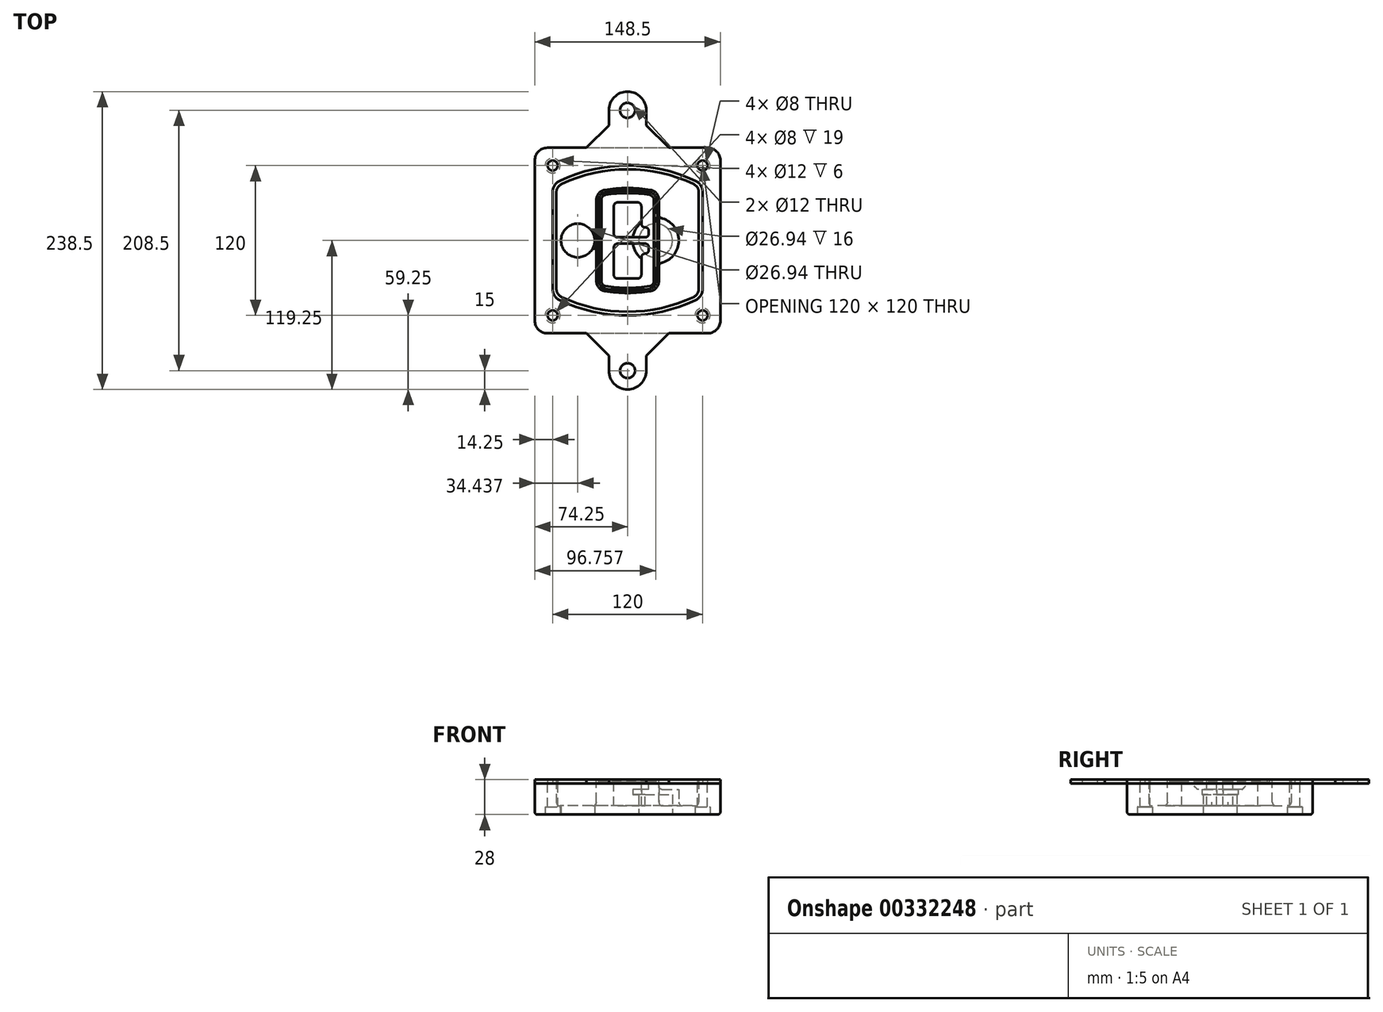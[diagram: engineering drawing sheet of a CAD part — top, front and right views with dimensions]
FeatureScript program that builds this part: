
annotation { "Feature Type Name" : "Feature", "Feature Type Description" : "" }
export const myFeature = defineFeature(function(context is Context, id is Id, definition is map)
    precondition{}
    {
        {
            var Q0;
            Q0=qCreatedBy(makeId("Top.planeOp"),FACE);
            var sketch = newSketch(context, id + "F0", { "sketchPlane" : qUnion([Q0])});
            skPoint(sketch, "E0.rect.middle", {"position": v(0, 0) * mm});
            skLineSegment(sketch, "E1.bottom", {"start": v(-64.25, -74.25) * mm, "end": v(64.25, -74.25) * mm});
            skLineSegment(sketch, "E1.top", {"start": v(-64.25, 74.25) * mm, "end": v(64.25, 74.25) * mm});
            skLineSegment(sketch, "E1.left", {"start": v(-74.25, -64.25) * mm, "end": v(-74.25, 64.25) * mm});
            skLineSegment(sketch, "E1.right", {"start": v(74.25, -64.25) * mm, "end": v(74.25, 64.25) * mm});
            skLineSegment(sketch, "E2", {"start": v(-74.25, 74.25) * mm, "end": v(74.25, -74.25) * mm, "construction": true});
            skLineSegment(sketch, "E3", {"start": v(74.25, 74.25) * mm, "end": v(-74.25, -74.25) * mm, "construction": true});
            skCircle(sketch, "E4", {"center": v(-60, 60) * mm, "radius": 4 * mm});
            skCircle(sketch, "E5", {"center": v(60, 60) * mm, "radius": 4 * mm});
            skCircle(sketch, "E6", {"center": v(60, -60) * mm, "radius": 4 * mm});
            skCircle(sketch, "E7", {"center": v(-60, -60) * mm, "radius": 4 * mm});
            skLineSegment(sketch, "E8", {"start": v(-60, 60) * mm, "end": v(60, 60) * mm, "construction": true});
            skLineSegment(sketch, "E9", {"start": v(60, 60) * mm, "end": v(60, -60) * mm, "construction": true});
            skLineSegment(sketch, "E10", {"start": v(60, -60) * mm, "end": v(-60, -60) * mm, "construction": true});
            skLineSegment(sketch, "E11", {"start": v(-60, -60) * mm, "end": v(-60, 60) * mm, "construction": true});
            skLineSegment(sketch, "E12", {"start": v(-60, 38.83) * mm, "end": v(-60, -38.83) * mm});
            skLineSegment(sketch, "E13", {"start": v(60, 38.83) * mm, "end": v(60, -38.83) * mm});
            skArc(sketch, "E14", {"start": v(54.26, 47.88) * mm, "mid": v(0, 60) * mm, "end": v(-54.26, 47.88) * mm});
            skArc(sketch, "E15", {"start": v(-54.26, -47.88) * mm, "mid": v(0, -60) * mm, "end": v(54.26, -47.88) * mm});
            skLineSegment(sketch, "E16", {"start": v(-60, 0) * mm, "end": v(60, 0) * mm, "construction": true});
            skPoint(sketch, "E17.visualSharp", {"position": v(-60, -45) * mm});
            skArc(sketch, "E17.filletArc", {"start": v(-60, -38.83) * mm, "mid": v(-58.44, -44.2) * mm, "end": v(-54.26, -47.88) * mm});
            skPoint(sketch, "E18.visualSharp", {"position": v(-60, 45) * mm});
            skArc(sketch, "E18.filletArc", {"start": v(-54.26, 47.88) * mm, "mid": v(-58.44, 44.2) * mm, "end": v(-60, 38.83) * mm});
            skPoint(sketch, "E19.visualSharp", {"position": v(60, 45) * mm});
            skArc(sketch, "E19.filletArc", {"start": v(60, 38.83) * mm, "mid": v(58.44, 44.2) * mm, "end": v(54.26, 47.88) * mm});
            skPoint(sketch, "E20.visualSharp", {"position": v(60, -45) * mm});
            skArc(sketch, "E20.filletArc", {"start": v(54.26, -47.88) * mm, "mid": v(58.44, -44.2) * mm, "end": v(60, -38.83) * mm});
            skPoint(sketch, "E21.visualSharp", {"position": v(-74.25, 74.25) * mm});
            skArc(sketch, "E21.filletArc", {"start": v(-64.25, 74.25) * mm, "mid": v(-71.32, 71.32) * mm, "end": v(-74.25, 64.25) * mm});
            skPoint(sketch, "E22.visualSharp", {"position": v(74.25, 74.25) * mm});
            skArc(sketch, "E22.filletArc", {"start": v(74.25, 64.25) * mm, "mid": v(71.32, 71.32) * mm, "end": v(64.25, 74.25) * mm});
            skPoint(sketch, "E23.visualSharp", {"position": v(74.25, -74.25) * mm});
            skArc(sketch, "E23.filletArc", {"start": v(64.25, -74.25) * mm, "mid": v(71.32, -71.32) * mm, "end": v(74.25, -64.25) * mm});
            skPoint(sketch, "E24.visualSharp", {"position": v(-74.25, -74.25) * mm});
            skArc(sketch, "E24.filletArc", {"start": v(-74.25, -64.25) * mm, "mid": v(-71.32, -71.32) * mm, "end": v(-64.25, -74.25) * mm});
            skArc(sketch, "E25.0", {"start": v(57, 38.83) * mm, "mid": v(55.9, 42.58) * mm, "end": v(52.98, 45.17) * mm});
            skLineSegment(sketch, "E25.1", {"start": v(57, 38.83) * mm, "end": v(57, -38.83) * mm});
            skArc(sketch, "E25.2", {"start": v(52.98, -45.17) * mm, "mid": v(55.9, -42.58) * mm, "end": v(57, -38.83) * mm});
            skArc(sketch, "E25.3", {"start": v(-52.98, -45.17) * mm, "mid": v(0, -57) * mm, "end": v(52.98, -45.17) * mm});
            skArc(sketch, "E25.4", {"start": v(-57, -38.83) * mm, "mid": v(-55.9, -42.58) * mm, "end": v(-52.98, -45.17) * mm});
            skArc(sketch, "E25.5", {"start": v(52.98, 45.17) * mm, "mid": v(0, 57) * mm, "end": v(-52.98, 45.17) * mm});
            skLineSegment(sketch, "E25.6", {"start": v(-57, 38.83) * mm, "end": v(-57, -38.83) * mm});
            skArc(sketch, "E25.7", {"start": v(-52.98, 45.17) * mm, "mid": v(-55.9, 42.58) * mm, "end": v(-57, 38.83) * mm});
            skArc(sketch, "E26.0", {"start": v(-55.96, 51.5) * mm, "mid": v(-61.82, 46.33) * mm, "end": v(-64, 38.83) * mm});
            skArc(sketch, "E26.1", {"start": v(55.96, 51.5) * mm, "mid": v(0, 64) * mm, "end": v(-55.96, 51.5) * mm});
            skArc(sketch, "E26.2", {"start": v(64, 38.83) * mm, "mid": v(61.82, 46.33) * mm, "end": v(55.96, 51.5) * mm});
            skLineSegment(sketch, "E26.3", {"start": v(64, 38.83) * mm, "end": v(64, -38.83) * mm});
            skArc(sketch, "E26.4", {"start": v(55.96, -51.5) * mm, "mid": v(61.82, -46.33) * mm, "end": v(64, -38.83) * mm});
            skLineSegment(sketch, "E26.5", {"start": v(-64, 38.83) * mm, "end": v(-64, -38.83) * mm});
            skArc(sketch, "E26.6", {"start": v(-55.96, -51.5) * mm, "mid": v(0, -64) * mm, "end": v(55.96, -51.5) * mm});
            skArc(sketch, "E26.7", {"start": v(-64, -38.83) * mm, "mid": v(-61.82, -46.33) * mm, "end": v(-55.96, -51.5) * mm});
            skSolve(sketch);
        }
        {
            var Q0;
            Q0=makeQuery(id+"F0.imprint","IMPRINT",FACE,{"disambiguationData":[TD([[makeQuery(id+"F0.imprint","IMPRINT",EDGE,{"derivedFrom":sQuery(id+"F0.wireOp",EDGE,"E1.bottom")}),1.0]])]});
            var Q1;
            Q1=makeQuery(id+"F0.imprint","IMPRINT",FACE,{"disambiguationData":[TD([[makeQuery(id+"F0.imprint","IMPRINT",EDGE,{"derivedFrom":sQuery(id+"F0.wireOp",EDGE,"E12")}),1.0]])]});
            var Q2;
            Q2=makeQuery(id+"F0.imprint","IMPRINT",FACE,{"disambiguationData":[TD([[makeQuery(id+"F0.imprint","IMPRINT",EDGE,{"derivedFrom":sQuery(id+"F0.wireOp",EDGE,"E25.0")}),1.0]])]});
            var Q3;
            Q3=makeQuery(id+"F0.imprint","IMPRINT",FACE,{"disambiguationData":[TD([[makeQuery(id+"F0.imprint","IMPRINT",EDGE,{"derivedFrom":sQuery(id+"F0.wireOp",EDGE,"E12")}),-1.0]])]});
            extrude(context, id + "F1", {"entities" : qUnion([Q0, Q1, Q2, Q3]), "oppositeDirection" : true, "depth" : 25 * mm});
        }
        {
            var Q0;
            Q0=makeQuery(id+"F0.imprint","IMPRINT",FACE,{"disambiguationData":[TD([[makeQuery(id+"F0.imprint","IMPRINT",EDGE,{"derivedFrom":sQuery(id+"F0.wireOp",EDGE,"E12")}),1.0]])]});
            extrude(context, id + "F2", {"entities" : qUnion([Q0]), "operationType" : NewBodyOperationType.ADD, "depth" : 3 * mm});
        }
        {
            var Q0;
            Q0=makeQuery(id+"F0.imprint","IMPRINT",FACE,{"disambiguationData":[TD([[makeQuery(id+"F0.imprint","IMPRINT",EDGE,{"derivedFrom":sQuery(id+"F0.wireOp",EDGE,"E25.0")}),1.0]])]});
            extrude(context, id + "F3", {"entities" : qUnion([Q0]), "operationType" : NewBodyOperationType.REMOVE, "oppositeDirection" : true, "depth" : 18 * mm});
        }
        {
            var Q0;
            Q0=makeQuery(id+"F2.opExtrude","CAP_FACE",FACE,{"disambiguationData":[OSD([sQuery(id+"F0.wireOp",EDGE,"E12"),sQuery(id+"F0.wireOp",EDGE,"E13"),sQuery(id+"F0.wireOp",EDGE,"E14"),sQuery(id+"F0.wireOp",EDGE,"E15"),sQuery(id+"F0.wireOp",EDGE,"E17.filletArc"),sQuery(id+"F0.wireOp",EDGE,"E18.filletArc"),sQuery(id+"F0.wireOp",EDGE,"E19.filletArc"),sQuery(id+"F0.wireOp",EDGE,"E20.filletArc"),sQuery(id+"F0.wireOp",EDGE,"E25.0"),sQuery(id+"F0.wireOp",EDGE,"E25.1"),sQuery(id+"F0.wireOp",EDGE,"E25.2"),sQuery(id+"F0.wireOp",EDGE,"E25.3"),sQuery(id+"F0.wireOp",EDGE,"E25.4"),sQuery(id+"F0.wireOp",EDGE,"E25.5"),sQuery(id+"F0.wireOp",EDGE,"E25.6"),sQuery(id+"F0.wireOp",EDGE,"E25.7")])],"isStart":false});
            var sketch = newSketch(context, id + "F4", { "sketchPlane" : qUnion([Q0])});
            skArc(sketch, "E27.0", {"start": v(-18.34, -40.45) * mm, "mid": v(0, -42) * mm, "end": v(18.34, -40.45) * mm});
            skArc(sketch, "E28.0", {"start": v(18.34, 40.45) * mm, "mid": v(0, 42) * mm, "end": v(-18.34, 40.45) * mm});
            skLineSegment(sketch, "E29", {"start": v(-25, 32.57) * mm, "end": v(-25, -32.57) * mm});
            skLineSegment(sketch, "E30", {"start": v(25, 32.57) * mm, "end": v(25, -32.57) * mm});
            skLineSegment(sketch, "E31", {"start": v(-25, 39.1) * mm, "end": v(25, 39.1) * mm, "construction": true});
            skLineSegment(sketch, "E32", {"start": v(-25, -39.1) * mm, "end": v(25, -39.1) * mm, "construction": true});
            skPoint(sketch, "E33.visualSharp", {"position": v(-25, 39.1) * mm});
            skArc(sketch, "E33.filletArc", {"start": v(-18.34, 40.45) * mm, "mid": v(-23.11, 37.73) * mm, "end": v(-25, 32.57) * mm});
            skPoint(sketch, "E34.visualSharp", {"position": v(25, 39.1) * mm});
            skArc(sketch, "E34.filletArc", {"start": v(25, 32.57) * mm, "mid": v(23.11, 37.73) * mm, "end": v(18.34, 40.45) * mm});
            skPoint(sketch, "E35.visualSharp", {"position": v(25, -39.1) * mm});
            skArc(sketch, "E35.filletArc", {"start": v(18.34, -40.45) * mm, "mid": v(23.11, -37.73) * mm, "end": v(25, -32.57) * mm});
            skPoint(sketch, "E36.visualSharp", {"position": v(-25, -39.1) * mm});
            skArc(sketch, "E36.filletArc", {"start": v(-25, -32.57) * mm, "mid": v(-23.11, -37.73) * mm, "end": v(-18.34, -40.45) * mm});
            skArc(sketch, "E37.0", {"start": v(52.98, 45.17) * mm, "mid": v(0, 57) * mm, "end": v(-52.98, 45.17) * mm});
            skArc(sketch, "E37.1", {"start": v(-52.98, 45.17) * mm, "mid": v(-55.9, 42.58) * mm, "end": v(-57, 38.83) * mm});
            skLineSegment(sketch, "E37.2", {"start": v(-57, 38.83) * mm, "end": v(-57, -38.83) * mm});
            skArc(sketch, "E37.3", {"start": v(-57, -38.83) * mm, "mid": v(-55.9, -42.58) * mm, "end": v(-52.98, -45.17) * mm});
            skArc(sketch, "E37.4", {"start": v(-52.98, -45.17) * mm, "mid": v(0, -57) * mm, "end": v(52.98, -45.17) * mm});
            skArc(sketch, "E37.5", {"start": v(52.98, -45.17) * mm, "mid": v(55.9, -42.58) * mm, "end": v(57, -38.83) * mm});
            skLineSegment(sketch, "E37.6", {"start": v(57, 38.83) * mm, "end": v(57, -38.83) * mm});
            skArc(sketch, "E37.7", {"start": v(57, 38.83) * mm, "mid": v(55.9, 42.58) * mm, "end": v(52.98, 45.17) * mm});
            skLineSegment(sketch, "E38.0", {"start": v(23, 32.57) * mm, "end": v(23, -32.57) * mm});
            skArc(sketch, "E38.1", {"start": v(18, -38.48) * mm, "mid": v(21.58, -36.44) * mm, "end": v(23, -32.57) * mm});
            skArc(sketch, "E38.2", {"start": v(-18, -38.48) * mm, "mid": v(0, -40) * mm, "end": v(18, -38.48) * mm});
            skArc(sketch, "E38.3", {"start": v(-23, -32.57) * mm, "mid": v(-21.58, -36.44) * mm, "end": v(-18, -38.48) * mm});
            skLineSegment(sketch, "E38.4", {"start": v(-23, 32.57) * mm, "end": v(-23, -32.57) * mm});
            skArc(sketch, "E38.5", {"start": v(23, 32.57) * mm, "mid": v(21.58, 36.44) * mm, "end": v(18, 38.48) * mm});
            skArc(sketch, "E38.6", {"start": v(-18, 38.48) * mm, "mid": v(-21.58, 36.44) * mm, "end": v(-23, 32.57) * mm});
            skArc(sketch, "E38.7", {"start": v(18, 38.48) * mm, "mid": v(0, 40) * mm, "end": v(-18, 38.48) * mm});
            skArc(sketch, "E39.0", {"start": v(21, 32.57) * mm, "mid": v(20.06, 35.15) * mm, "end": v(17.67, 36.5) * mm});
            skLineSegment(sketch, "E39.1", {"start": v(21, 32.57) * mm, "end": v(21, -32.57) * mm});
            skArc(sketch, "E39.2", {"start": v(17.67, -36.5) * mm, "mid": v(20.06, -35.15) * mm, "end": v(21, -32.57) * mm});
            skArc(sketch, "E39.3", {"start": v(-17.67, -36.5) * mm, "mid": v(0, -38) * mm, "end": v(17.67, -36.5) * mm});
            skArc(sketch, "E39.4", {"start": v(-21, -32.57) * mm, "mid": v(-20.06, -35.15) * mm, "end": v(-17.67, -36.5) * mm});
            skArc(sketch, "E39.5", {"start": v(17.67, 36.5) * mm, "mid": v(0, 38) * mm, "end": v(-17.67, 36.5) * mm});
            skLineSegment(sketch, "E39.6", {"start": v(-21, 32.57) * mm, "end": v(-21, -32.57) * mm});
            skArc(sketch, "E39.7", {"start": v(-17.67, 36.5) * mm, "mid": v(-20.06, 35.15) * mm, "end": v(-21, 32.57) * mm});
            skLineSegment(sketch, "E40", {"start": v(-25, 0) * mm, "end": v(25, 0) * mm, "construction": true});
            skLineSegment(sketch, "E41", {"start": v(-11, 5.5) * mm, "end": v(-11, 27.5) * mm});
            skLineSegment(sketch, "E42", {"start": v(-8, 30.5) * mm, "end": v(8, 30.5) * mm});
            skLineSegment(sketch, "E43", {"start": v(11, 27.5) * mm, "end": v(11, 13.5) * mm});
            skLineSegment(sketch, "E44", {"start": v(14, 10.5) * mm, "end": v(14, 10.5) * mm});
            skLineSegment(sketch, "E45", {"start": v(17, 7.5) * mm, "end": v(17, 5.5) * mm});
            skLineSegment(sketch, "E46", {"start": v(14, 2.5) * mm, "end": v(-8, 2.5) * mm});
            skPoint(sketch, "E47.visualSharp", {"position": v(-11, 30.5) * mm});
            skArc(sketch, "E47.filletArc", {"start": v(-8, 30.5) * mm, "mid": v(-10.12, 29.62) * mm, "end": v(-11, 27.5) * mm});
            skPoint(sketch, "E48.visualSharp", {"position": v(11, 30.5) * mm});
            skArc(sketch, "E48.filletArc", {"start": v(11, 27.5) * mm, "mid": v(10.12, 29.62) * mm, "end": v(8, 30.5) * mm});
            skPoint(sketch, "E49.visualSharp", {"position": v(11, 10.5) * mm});
            skArc(sketch, "E49.filletArc", {"start": v(11, 13.5) * mm, "mid": v(11.88, 11.38) * mm, "end": v(14, 10.5) * mm});
            skPoint(sketch, "E50.visualSharp", {"position": v(17, 10.5) * mm});
            skArc(sketch, "E50.filletArc", {"start": v(17, 7.5) * mm, "mid": v(16.12, 9.62) * mm, "end": v(14, 10.5) * mm});
            skPoint(sketch, "E51.visualSharp", {"position": v(17, 2.5) * mm});
            skArc(sketch, "E51.filletArc", {"start": v(14, 2.5) * mm, "mid": v(16.12, 3.38) * mm, "end": v(17, 5.5) * mm});
            skPoint(sketch, "E52.visualSharp", {"position": v(-11, 2.5) * mm});
            skArc(sketch, "E52.filletArc", {"start": v(-11, 5.5) * mm, "mid": v(-10.12, 3.38) * mm, "end": v(-8, 2.5) * mm});
            skLineSegment(sketch, "E53.0.MirrorCS", {"start": v(14, -2.5) * mm, "end": v(-8, -2.5) * mm});
            skArc(sketch, "E54.0.MirrorCS", {"start": v(-11, -5.5) * mm, "mid": v(-10.12, -3.38) * mm, "end": v(-8, -2.5) * mm});
            skLineSegment(sketch, "E55.0.MirrorCS", {"start": v(-11, -5.5) * mm, "end": v(-11, -27.5) * mm});
            skArc(sketch, "E56.0.MirrorCS", {"start": v(-8, -30.5) * mm, "mid": v(-10.12, -29.62) * mm, "end": v(-11, -27.5) * mm});
            skLineSegment(sketch, "E57.0.MirrorCS", {"start": v(-8, -30.5) * mm, "end": v(8, -30.5) * mm});
            skArc(sketch, "E58.0.MirrorCS", {"start": v(11, -27.5) * mm, "mid": v(10.12, -29.62) * mm, "end": v(8, -30.5) * mm});
            skLineSegment(sketch, "E59.0.MirrorCS", {"start": v(11, -27.5) * mm, "end": v(11, -13.5) * mm});
            skArc(sketch, "E60.0.MirrorCS", {"start": v(11, -13.5) * mm, "mid": v(11.88, -11.38) * mm, "end": v(14, -10.5) * mm});
            skArc(sketch, "E61.0.MirrorCS", {"start": v(17, -7.5) * mm, "mid": v(16.12, -9.62) * mm, "end": v(14, -10.5) * mm});
            skLineSegment(sketch, "E62.0.MirrorCS", {"start": v(17, -7.5) * mm, "end": v(17, -5.5) * mm});
            skArc(sketch, "E63.0.MirrorCS", {"start": v(14, -2.5) * mm, "mid": v(16.12, -3.38) * mm, "end": v(17, -5.5) * mm});
            skSolve(sketch);
        }
        {
            var Q0;
            Q0=makeQuery(id+"F4.imprint","IMPRINT",FACE,{"disambiguationData":[TD([[makeQuery(id+"F4.imprint","IMPRINT",EDGE,{"derivedFrom":sQuery(id+"F4.wireOp",EDGE,"E27.0")}),1.0]])]});
            var Q1;
            Q1=makeQuery(id+"F4.imprint","IMPRINT",FACE,{"disambiguationData":[TD([[makeQuery(id+"F4.imprint","IMPRINT",EDGE,{"derivedFrom":sQuery(id+"F4.wireOp",EDGE,"E38.0")}),-1.0]])]});
            var Q2;
            Q2=makeQuery(id+"F4.imprint","IMPRINT",FACE,{"disambiguationData":[TD([[makeQuery(id+"F4.imprint","IMPRINT",EDGE,{"derivedFrom":sQuery(id+"F4.wireOp",EDGE,"E39.0")}),1.0]])]});
            extrude(context, id + "F5", {"entities" : qUnion([Q0, Q1, Q2]), "operationType" : NewBodyOperationType.ADD, "endBound" : BoundingType.UP_TO_NEXT, "oppositeDirection" : true, "depth" : 25 * mm});
        }
        {
            var Q0;
            Q0=makeQuery(id+"F4.imprint","IMPRINT",FACE,{"disambiguationData":[TD([[makeQuery(id+"F4.imprint","IMPRINT",EDGE,{"derivedFrom":sQuery(id+"F4.wireOp",EDGE,"E38.0")}),-1.0]])]});
            extrude(context, id + "F6", {"entities" : qUnion([Q0]), "operationType" : NewBodyOperationType.REMOVE, "oppositeDirection" : true, "depth" : 2 * mm});
        }
        {
            var Q0;
            Q0=makeQuery(id+"F1.opExtrude","CAP_FACE",FACE,{"disambiguationData":[OSD([sQuery(id+"F0.wireOp",EDGE,"E1.bottom"),sQuery(id+"F0.wireOp",EDGE,"E1.top"),sQuery(id+"F0.wireOp",EDGE,"E1.left"),sQuery(id+"F0.wireOp",EDGE,"E1.right"),sQuery(id+"F0.wireOp",EDGE,"E4"),sQuery(id+"F0.wireOp",EDGE,"E5"),sQuery(id+"F0.wireOp",EDGE,"E6"),sQuery(id+"F0.wireOp",EDGE,"E7"),sQuery(id+"F0.wireOp",EDGE,"E21.filletArc"),sQuery(id+"F0.wireOp",EDGE,"E22.filletArc"),sQuery(id+"F0.wireOp",EDGE,"E23.filletArc"),sQuery(id+"F0.wireOp",EDGE,"E24.filletArc")])],"isStart":false});
            var sketch = newSketch(context, id + "F7", { "sketchPlane" : qUnion([Q0])});
            skCircle(sketch, "E64", {"center": v(22.5, 0) * mm, "radius": 13.47 * mm});
            skCircle(sketch, "E65", {"center": v(-39.81, 0) * mm, "radius": 13.47 * mm});
            skLineSegment(sketch, "E66", {"start": v(74.25, 0) * mm, "end": v(-74.25, 0) * mm});
            skCircle(sketch, "E67", {"center": v(22.5, 0) * mm, "radius": 18.47 * mm});
            skCircle(sketch, "E68", {"center": v(60, -60) * mm, "radius": 6 * mm});
            skCircle(sketch, "E69", {"center": v(-60, -60) * mm, "radius": 6 * mm});
            skCircle(sketch, "E70", {"center": v(-60, 60) * mm, "radius": 6 * mm});
            skCircle(sketch, "E71", {"center": v(60, 60) * mm, "radius": 6 * mm});
            skSolve(sketch);
        }
        {
            var Q0;
            {var subQ1=sQuery(id+"F7.wireOp",EDGE,"E66");var subQ4=sQuery(id+"F7.wireOp",EDGE,"E64");var subQ6=makeQuery(id+"F7.imprint","INTERSECT",VERTEX,{"disambiguationData":[OD(0.0)],"derivedFrom":[subQ4,subQ1]});Q0=makeQuery(id+"F7.imprint","IMPRINT",FACE,{"disambiguationData":[TD([[makeQuery(id+"F7.imprint","IMPRINT",EDGE,{"disambiguationData":[TD([[subQ6,-1.0]])],"derivedFrom":subQ4}),-1.0]])]});}
            var Q1;
            {var subQ0=sQuery(id+"F7.wireOp",EDGE,"E66");var subQ1=sQuery(id+"F7.wireOp",EDGE,"E64");var subQ3=makeQuery(id+"F7.imprint","INTERSECT",VERTEX,{"disambiguationData":[OD(0.0)],"derivedFrom":[subQ1,subQ0]});Q1=makeQuery(id+"F7.imprint","IMPRINT",FACE,{"disambiguationData":[TD([[makeQuery(id+"F7.imprint","IMPRINT",EDGE,{"disambiguationData":[TD([[subQ3,-1.0]])],"derivedFrom":subQ1}),1.0]])]});}
            var Q2;
            {var subQ0=sQuery(id+"F7.wireOp",EDGE,"E66");var subQ1=sQuery(id+"F7.wireOp",EDGE,"E64");var subQ3=makeQuery(id+"F7.imprint","INTERSECT",VERTEX,{"disambiguationData":[OD(0.0)],"derivedFrom":[subQ1,subQ0]});Q2=makeQuery(id+"F7.imprint","IMPRINT",FACE,{"disambiguationData":[TD([[makeQuery(id+"F7.imprint","IMPRINT",EDGE,{"disambiguationData":[TD([[subQ3,1.0]])],"derivedFrom":subQ1}),1.0]])]});}
            var Q3;
            {var subQ1=sQuery(id+"F7.wireOp",EDGE,"E66");var subQ4=sQuery(id+"F7.wireOp",EDGE,"E64");var subQ6=makeQuery(id+"F7.imprint","INTERSECT",VERTEX,{"disambiguationData":[OD(0.0)],"derivedFrom":[subQ4,subQ1]});Q3=makeQuery(id+"F7.imprint","IMPRINT",FACE,{"disambiguationData":[TD([[makeQuery(id+"F7.imprint","IMPRINT",EDGE,{"disambiguationData":[TD([[subQ6,1.0]])],"derivedFrom":subQ4}),-1.0]])]});}
            extrude(context, id + "F8", {"entities" : qUnion([Q0, Q1, Q2, Q3]), "operationType" : NewBodyOperationType.ADD, "oppositeDirection" : true, "depth" : 20 * mm});
        }
        {
            var Q0;
            {var subQ0=sQuery(id+"F7.wireOp",EDGE,"E66");var subQ1=sQuery(id+"F7.wireOp",EDGE,"E64");var subQ3=makeQuery(id+"F7.imprint","INTERSECT",VERTEX,{"disambiguationData":[OD(0.0)],"derivedFrom":[subQ1,subQ0]});Q0=makeQuery(id+"F7.imprint","IMPRINT",FACE,{"disambiguationData":[TD([[makeQuery(id+"F7.imprint","IMPRINT",EDGE,{"disambiguationData":[TD([[subQ3,-1.0]])],"derivedFrom":subQ1}),1.0]])]});}
            var Q1;
            {var subQ0=sQuery(id+"F7.wireOp",EDGE,"E66");var subQ1=sQuery(id+"F7.wireOp",EDGE,"E64");var subQ3=makeQuery(id+"F7.imprint","INTERSECT",VERTEX,{"disambiguationData":[OD(0.0)],"derivedFrom":[subQ1,subQ0]});Q1=makeQuery(id+"F7.imprint","IMPRINT",FACE,{"disambiguationData":[TD([[makeQuery(id+"F7.imprint","IMPRINT",EDGE,{"disambiguationData":[TD([[subQ3,1.0]])],"derivedFrom":subQ1}),1.0]])]});}
            extrude(context, id + "F9", {"entities" : qUnion([Q0, Q1]), "operationType" : NewBodyOperationType.REMOVE, "oppositeDirection" : true, "depth" : 16 * mm});
        }
        {
            var Q0;
            {var subQ0=sQuery(id+"F7.wireOp",EDGE,"E66");var subQ1=sQuery(id+"F7.wireOp",EDGE,"E65");var subQ3=makeQuery(id+"F7.imprint","INTERSECT",VERTEX,{"disambiguationData":[OD(0.0)],"derivedFrom":[subQ1,subQ0]});Q0=makeQuery(id+"F7.imprint","IMPRINT",FACE,{"disambiguationData":[TD([[makeQuery(id+"F7.imprint","IMPRINT",EDGE,{"disambiguationData":[TD([[subQ3,-1.0]])],"derivedFrom":subQ1}),1.0]])]});}
            var Q1;
            {var subQ0=sQuery(id+"F7.wireOp",EDGE,"E66");var subQ1=sQuery(id+"F7.wireOp",EDGE,"E65");var subQ3=makeQuery(id+"F7.imprint","INTERSECT",VERTEX,{"disambiguationData":[OD(0.0)],"derivedFrom":[subQ1,subQ0]});Q1=makeQuery(id+"F7.imprint","IMPRINT",FACE,{"disambiguationData":[TD([[makeQuery(id+"F7.imprint","IMPRINT",EDGE,{"disambiguationData":[TD([[subQ3,1.0]])],"derivedFrom":subQ1}),1.0]])]});}
            extrude(context, id + "F10", {"entities" : qUnion([Q0, Q1]), "operationType" : NewBodyOperationType.REMOVE, "oppositeDirection" : true, "depth" : 25 * mm});
        }
        {
            var Q0;
            Q0=makeQuery(id+"F7.imprint","IMPRINT",FACE,{"disambiguationData":[TD([[makeQuery(id+"F7.imprint","IMPRINT",EDGE,{"derivedFrom":sQuery(id+"F7.wireOp",EDGE,"E68")}),1.0]])]});
            var Q1;
            Q1=makeQuery(id+"F7.imprint","IMPRINT",FACE,{"disambiguationData":[TD([[makeQuery(id+"F7.imprint","IMPRINT",EDGE,{"derivedFrom":makeQuery(id+"F1.opExtrude","CAP_EDGE",EDGE,{"disambiguationData":[OSD([sQuery(id+"F0.wireOp",EDGE,"E5")])],"isStart":false})}),-1.0]])]});
            var Q2;
            Q2=makeQuery(id+"F7.imprint","IMPRINT",FACE,{"disambiguationData":[TD([[makeQuery(id+"F7.imprint","IMPRINT",EDGE,{"derivedFrom":sQuery(id+"F7.wireOp",EDGE,"E69")}),1.0]])]});
            var Q3;
            Q3=makeQuery(id+"F7.imprint","IMPRINT",FACE,{"disambiguationData":[TD([[makeQuery(id+"F7.imprint","IMPRINT",EDGE,{"derivedFrom":makeQuery(id+"F1.opExtrude","CAP_EDGE",EDGE,{"disambiguationData":[OSD([sQuery(id+"F0.wireOp",EDGE,"E4")])],"isStart":false})}),-1.0]])]});
            var Q4;
            Q4=makeQuery(id+"F7.imprint","IMPRINT",FACE,{"disambiguationData":[TD([[makeQuery(id+"F7.imprint","IMPRINT",EDGE,{"derivedFrom":sQuery(id+"F7.wireOp",EDGE,"E70")}),1.0]])]});
            var Q5;
            Q5=makeQuery(id+"F7.imprint","IMPRINT",FACE,{"disambiguationData":[TD([[makeQuery(id+"F7.imprint","IMPRINT",EDGE,{"derivedFrom":makeQuery(id+"F1.opExtrude","CAP_EDGE",EDGE,{"disambiguationData":[OSD([sQuery(id+"F0.wireOp",EDGE,"E7")])],"isStart":false})}),-1.0]])]});
            var Q6;
            Q6=makeQuery(id+"F7.imprint","IMPRINT",FACE,{"disambiguationData":[TD([[makeQuery(id+"F7.imprint","IMPRINT",EDGE,{"derivedFrom":sQuery(id+"F7.wireOp",EDGE,"E71")}),1.0]])]});
            var Q7;
            Q7=makeQuery(id+"F7.imprint","IMPRINT",FACE,{"disambiguationData":[TD([[makeQuery(id+"F7.imprint","IMPRINT",EDGE,{"derivedFrom":makeQuery(id+"F1.opExtrude","CAP_EDGE",EDGE,{"disambiguationData":[OSD([sQuery(id+"F0.wireOp",EDGE,"E6")])],"isStart":false})}),-1.0]])]});
            extrude(context, id + "F11", {"entities" : qUnion([Q0, Q1, Q2, Q3, Q4, Q5, Q6, Q7]), "operationType" : NewBodyOperationType.REMOVE, "oppositeDirection" : true, "depth" : 6 * mm});
        }
        {
            var Q0;
            Q0=makeQuery(id+"F9.boolean.opBoolean","COPY",FACE,{"derivedFrom":makeQuery(id+"F9.opExtrude","CAP_FACE",FACE,{"disambiguationData":[OSD([sQuery(id+"F7.wireOp",EDGE,"E64")])],"isStart":false})});
            var sketch = newSketch(context, id + "F12", { "sketchPlane" : qUnion([Q0])});
            skArc(sketch, "E72.0", {"start": v(11, 14.45) * mm, "mid": v(6.45, 9.13) * mm, "end": v(4.2, 2.5) * mm});
            skArc(sketch, "E72.1", {"start": v(4.2, -2.5) * mm, "mid": v(6.45, -9.13) * mm, "end": v(11, -14.45) * mm});
            skLineSegment(sketch, "E73", {"start": v(4.2, -2.5) * mm, "end": v(14, -2.5) * mm});
            skLineSegment(sketch, "E74.0", {"start": v(14, 2.5) * mm, "end": v(4.2, 2.5) * mm});
            skArc(sketch, "E74.1", {"start": v(14, 2.5) * mm, "mid": v(16.12, 3.38) * mm, "end": v(17, 5.5) * mm});
            skLineSegment(sketch, "E74.2", {"start": v(17, 7.5) * mm, "end": v(17, 5.5) * mm});
            skArc(sketch, "E74.3", {"start": v(17, 7.5) * mm, "mid": v(16.12, 9.62) * mm, "end": v(14, 10.5) * mm});
            skArc(sketch, "E74.4", {"start": v(11, 13.5) * mm, "mid": v(11.88, 11.38) * mm, "end": v(14, 10.5) * mm});
            skLineSegment(sketch, "E74.5", {"start": v(11, 14.45) * mm, "end": v(11, 13.5) * mm});
            skLineSegment(sketch, "E74.7", {"start": v(14, -2.5) * mm, "end": v(4.2, -2.5) * mm});
            skArc(sketch, "E74.8", {"start": v(14, -2.5) * mm, "mid": v(16.12, -3.38) * mm, "end": v(17, -5.5) * mm});
            skLineSegment(sketch, "E74.9", {"start": v(17, -7.5) * mm, "end": v(17, -5.5) * mm});
            skArc(sketch, "E74.10", {"start": v(17, -7.5) * mm, "mid": v(16.12, -9.62) * mm, "end": v(14, -10.5) * mm});
            skArc(sketch, "E74.11", {"start": v(11, -13.5) * mm, "mid": v(11.88, -11.38) * mm, "end": v(14, -10.5) * mm});
            skLineSegment(sketch, "E74.12", {"start": v(11, -14.45) * mm, "end": v(11, -13.5) * mm});
            skPoint(sketch, "E75.orphan", {"position": v(11, -27.5) * mm});
            skPoint(sketch, "E76.orphan", {"position": v(-8, -2.5) * mm});
            skPoint(sketch, "E77.orphan", {"position": v(-8, 2.5) * mm});
            skPoint(sketch, "E78.orphan", {"position": v(11, 27.5) * mm});
            skSolve(sketch);
        }
        {
            var Q0;
            {var subQ7=sQuery(id+"F12.wireOp",EDGE,"E72.0");var subQ14=sQuery(id+"F12.wireOp",EDGE,"E72.1");var subQ16=sQuery(id+"F12.wireOp",EDGE,"E74.1");var subQ18=sQuery(id+"F12.wireOp",EDGE,"E74.8");Q0=qUnion([makeQuery(id+"F12.imprint","IMPRINT",FACE,{"disambiguationData":[TD([[makeQuery(id+"F12.imprint","IMPRINT",EDGE,{"derivedFrom":subQ7}),1.0]])]}),makeQuery(id+"F12.imprint","IMPRINT",FACE,{"disambiguationData":[TD([[makeQuery(id+"F12.imprint","IMPRINT",EDGE,{"derivedFrom":subQ14}),1.0]])]}),makeQuery(id+"F12.imprint","IMPRINT",FACE,{"disambiguationData":[TD([[makeQuery(id+"F12.imprint","IMPRINT",EDGE,{"derivedFrom":subQ16}),1.0]])]}),makeQuery(id+"F12.imprint","IMPRINT",FACE,{"disambiguationData":[TD([[makeQuery(id+"F12.imprint","IMPRINT",EDGE,{"derivedFrom":subQ18}),-1.0]])]})]);}
            var Q1;
            Q1=makeQuery(id+"F5.boolean.opBoolean","SPLIT",FACE,{"disambiguationData":[TD([makeQuery(id+"F5.opExtrude","SWEPT_FACE",FACE,{"disambiguationData":[OSD([sQuery(id+"F4.wireOp",EDGE,"E41")])]})])],"derivedFrom":makeQuery(id+"F3.boolean.opBoolean","COPY",FACE,{"derivedFrom":makeQuery(id+"F3.opExtrude","CAP_FACE",FACE,{"disambiguationData":[OSD([sQuery(id+"F0.wireOp",EDGE,"E25.0"),sQuery(id+"F0.wireOp",EDGE,"E25.1"),sQuery(id+"F0.wireOp",EDGE,"E25.2"),sQuery(id+"F0.wireOp",EDGE,"E25.3"),sQuery(id+"F0.wireOp",EDGE,"E25.4"),sQuery(id+"F0.wireOp",EDGE,"E25.5"),sQuery(id+"F0.wireOp",EDGE,"E25.6"),sQuery(id+"F0.wireOp",EDGE,"E25.7")])],"isStart":false})})});
            extrude(context, id + "F13", {"entities" : qUnion([Q0]), "operationType" : NewBodyOperationType.REMOVE, "endBound" : BoundingType.UP_TO_SURFACE, "endBoundEntityFace" : qUnion([Q1]), "depth" : 25 * mm});
        }
        {
            var Q0;
            Q0=makeQuery(id+"F3.boolean.opBoolean","COPY",EDGE,{"derivedFrom":makeQuery(id+"F3.opExtrude","CAP_EDGE",EDGE,{"disambiguationData":[OSD([sQuery(id+"F0.wireOp",EDGE,"E25.6")])],"isStart":false})});
            var Q1;
            Q1=makeQuery(id+"F8.boolean.opBoolean","INTERSECT",EDGE,{"derivedFrom":[makeQuery(id+"F5.opExtrude","SWEPT_FACE",FACE,{"disambiguationData":[OSD([sQuery(id+"F4.wireOp",EDGE,"E30")])]}),makeQuery(id+"F8.opExtrude","CAP_FACE",FACE,{"disambiguationData":[OSD([sQuery(id+"F7.wireOp",EDGE,"E67")])],"isStart":false})]});
            var Q2;
            Q2=makeQuery(id+"F8.boolean.opBoolean","INTERSECT",EDGE,{"disambiguationData":[OD(1.0)],"derivedFrom":[makeQuery(id+"F5.opExtrude","SWEPT_FACE",FACE,{"disambiguationData":[OSD([sQuery(id+"F4.wireOp",EDGE,"E30")])]}),makeQuery(id+"F8.opExtrude","SWEPT_FACE",FACE,{"disambiguationData":[OSD([sQuery(id+"F7.wireOp",EDGE,"E67")])]})]});
            var Q3;
            {var subQ0=sQuery(id+"F4.wireOp",EDGE,"E30");Q3=makeQuery(id+"F8.boolean.opBoolean","SPLIT",EDGE,{"disambiguationData":[TD([makeQuery(id+"F5.opExtrude","SWEPT_FACE",FACE,{"disambiguationData":[OSD([sQuery(id+"F4.wireOp",EDGE,"E35.filletArc")])]})])],"derivedFrom":makeQuery(id+"F5.opExtrude","CAP_EDGE",EDGE,{"disambiguationData":[OSD([subQ0])],"isStart":false})});}
            var Q4;
            {var subQ0=sQuery(id+"F0.wireOp",EDGE,"E25.7");var subQ1=sQuery(id+"F0.wireOp",EDGE,"E25.1");var subQ2=sQuery(id+"F0.wireOp",EDGE,"E25.6");var subQ3=sQuery(id+"F0.wireOp",EDGE,"E25.5");var subQ4=sQuery(id+"F0.wireOp",EDGE,"E25.4");var subQ5=sQuery(id+"F0.wireOp",EDGE,"E25.0");var subQ6=sQuery(id+"F0.wireOp",EDGE,"E25.2");var subQ7=sQuery(id+"F0.wireOp",EDGE,"E25.3");Q4=makeQuery(id+"F8.boolean.opBoolean","INTERSECT",EDGE,{"derivedFrom":[makeQuery(id+"F5.boolean.opBoolean","SPLIT",FACE,{"disambiguationData":[TD([makeQuery(id+"F2.opExtrude","SWEPT_FACE",FACE,{"disambiguationData":[OSD([subQ5])]})])],"derivedFrom":makeQuery(id+"F3.boolean.opBoolean","COPY",FACE,{"derivedFrom":makeQuery(id+"F3.opExtrude","CAP_FACE",FACE,{"disambiguationData":[OSD([subQ5,subQ1,subQ6,subQ7,subQ4,subQ3,subQ2,subQ0])],"isStart":false})})}),makeQuery(id+"F8.opExtrude","SWEPT_FACE",FACE,{"disambiguationData":[OSD([sQuery(id+"F7.wireOp",EDGE,"E67")])]})]});}
            var Q5;
            Q5=makeQuery(id+"F8.boolean.opBoolean","INTERSECT",EDGE,{"disambiguationData":[OD(0.0)],"derivedFrom":[makeQuery(id+"F5.opExtrude","SWEPT_FACE",FACE,{"disambiguationData":[OSD([sQuery(id+"F4.wireOp",EDGE,"E30")])]}),makeQuery(id+"F8.opExtrude","SWEPT_FACE",FACE,{"disambiguationData":[OSD([sQuery(id+"F7.wireOp",EDGE,"E67")])]})]});
            fillet(context, id + "F14", {"entities" : qUnion([Q0, Q1, Q2, Q3, Q4, Q5]), "radius" : 3 * mm, "tangentPropagation" : true, "allowEdgeOverflow" : false});
        }
        {
            var Q0;
            Q0=makeQuery(id+"F1.opExtrude","CAP_EDGE",EDGE,{"disambiguationData":[OSD([sQuery(id+"F0.wireOp",EDGE,"E1.bottom")])],"isStart":false});
            fillet(context, id + "F15", {"entities" : qUnion([Q0]), "radius" : 2 * mm, "tangentPropagation" : true, "allowEdgeOverflow" : false});
        }
        {
            var Q0;
            {var subQ0=sQuery(id+"F0.wireOp",EDGE,"E21.filletArc");var subQ1=sQuery(id+"F0.wireOp",EDGE,"E7");var subQ2=sQuery(id+"F0.wireOp",EDGE,"E6");var subQ3=sQuery(id+"F0.wireOp",EDGE,"E5");var subQ4=sQuery(id+"F0.wireOp",EDGE,"E4");var subQ5=sQuery(id+"F0.wireOp",EDGE,"E22.filletArc");var subQ6=sQuery(id+"F0.wireOp",EDGE,"E1.bottom");var subQ7=sQuery(id+"F0.wireOp",EDGE,"E1.right");var subQ8=sQuery(id+"F0.wireOp",EDGE,"E1.top");var subQ9=sQuery(id+"F0.wireOp",EDGE,"E1.left");var subQ10=sQuery(id+"F0.wireOp",EDGE,"E23.filletArc");var subQ11=sQuery(id+"F0.wireOp",EDGE,"E24.filletArc");Q0=makeQuery(id+"F2.boolean.opBoolean","SPLIT",FACE,{"disambiguationData":[TD([makeQuery(id+"F1.opExtrude","SWEPT_FACE",FACE,{"disambiguationData":[OSD([subQ6])]})])],"derivedFrom":makeQuery(id+"F1.opExtrude","CAP_FACE",FACE,{"disambiguationData":[OSD([subQ6,subQ8,subQ9,subQ7,subQ4,subQ3,subQ2,subQ1,subQ0,subQ5,subQ10,subQ11])],"isStart":true})});}
            var sketch = newSketch(context, id + "F16", { "sketchPlane" : qUnion([Q0])});
            skLineSegment(sketch, "E79", {"start": v(0, 74.25) * mm, "end": v(0, 104.25) * mm, "construction": true});
            skLineSegment(sketch, "E80", {"start": v(-33, 74.25) * mm, "end": v(-15, 92.25) * mm});
            skLineSegment(sketch, "E81", {"start": v(15, 104.25) * mm, "end": v(15, 92.25) * mm});
            skLineSegment(sketch, "E82", {"start": v(-15, 92.25) * mm, "end": v(-15, 104.25) * mm});
            skArc(sketch, "E83", {"start": v(15, 104.25) * mm, "mid": v(0, 119.25) * mm, "end": v(-15, 104.25) * mm});
            skCircle(sketch, "E84", {"center": v(0, 104.25) * mm, "radius": 6 * mm});
            skLineSegment(sketch, "E85", {"start": v(15, 92.25) * mm, "end": v(33, 74.25) * mm});
            skLineSegment(sketch, "E86", {"start": v(-74.25, 0) * mm, "end": v(74.25, 0) * mm, "construction": true});
            skLineSegment(sketch, "E87.MirrorCS", {"start": v(-33, -74.25) * mm, "end": v(-15, -92.25) * mm});
            skLineSegment(sketch, "E88.MirrorCS", {"start": v(-15, -92.25) * mm, "end": v(-15, -104.25) * mm});
            skLineSegment(sketch, "E89.MirrorCS", {"start": v(0, -74.25) * mm, "end": v(0, -104.25) * mm, "construction": true});
            skArc(sketch, "E90.MirrorCS", {"start": v(15, -104.25) * mm, "mid": v(0, -119.25) * mm, "end": v(-15, -104.25) * mm});
            skLineSegment(sketch, "E91.MirrorCS", {"start": v(15, -104.25) * mm, "end": v(15, -92.25) * mm});
            skLineSegment(sketch, "E92.MirrorCS", {"start": v(15, -92.25) * mm, "end": v(33, -74.25) * mm});
            skCircle(sketch, "E93.MirrorC", {"center": v(0, -104.25) * mm, "radius": 6 * mm});
            skSolve(sketch);
        }
        {
            var Q0;
            {var subQ0=sQuery(id+"F16.wireOp",EDGE,"E80");Q0=makeQuery(id+"F16.imprint","IMPRINT",FACE,{"disambiguationData":[TD([[makeQuery(id+"F16.imprint","IMPRINT",EDGE,{"derivedFrom":subQ0}),-1.0]])]});}
            var Q1;
            {var subQ0=sQuery(id+"F16.wireOp",EDGE,"E87.MirrorCS");Q1=makeQuery(id+"F16.imprint","IMPRINT",FACE,{"disambiguationData":[TD([[makeQuery(id+"F16.imprint","IMPRINT",EDGE,{"derivedFrom":subQ0}),1.0]])]});}
            var Q2;
            Q2=makeQuery(id+"F16.imprint","IMPRINT",FACE,{"disambiguationData":[TD([[makeQuery(id+"F16.imprint","IMPRINT",EDGE,{"derivedFrom":makeQuery(id+"F1.opExtrude","CAP_EDGE",EDGE,{"disambiguationData":[OSD([sQuery(id+"F0.wireOp",EDGE,"E1.left")])],"isStart":true})}),-1.0]])]});
            var Q3;
            Q3=makeQuery(id+"F2.opExtrude","CAP_FACE",FACE,{"disambiguationData":[OSD([sQuery(id+"F0.wireOp",EDGE,"E12"),sQuery(id+"F0.wireOp",EDGE,"E13"),sQuery(id+"F0.wireOp",EDGE,"E14"),sQuery(id+"F0.wireOp",EDGE,"E15"),sQuery(id+"F0.wireOp",EDGE,"E17.filletArc"),sQuery(id+"F0.wireOp",EDGE,"E18.filletArc"),sQuery(id+"F0.wireOp",EDGE,"E19.filletArc"),sQuery(id+"F0.wireOp",EDGE,"E20.filletArc"),sQuery(id+"F0.wireOp",EDGE,"E25.0"),sQuery(id+"F0.wireOp",EDGE,"E25.1"),sQuery(id+"F0.wireOp",EDGE,"E25.2"),sQuery(id+"F0.wireOp",EDGE,"E25.3"),sQuery(id+"F0.wireOp",EDGE,"E25.4"),sQuery(id+"F0.wireOp",EDGE,"E25.5"),sQuery(id+"F0.wireOp",EDGE,"E25.6"),sQuery(id+"F0.wireOp",EDGE,"E25.7")])],"isStart":false});
            extrude(context, id + "F17", {"entities" : qUnion([Q0, Q1, Q2]), "endBound" : BoundingType.UP_TO_SURFACE, "endBoundEntityFace" : qUnion([Q3]), "depth" : 25 * mm});
        }
    });
